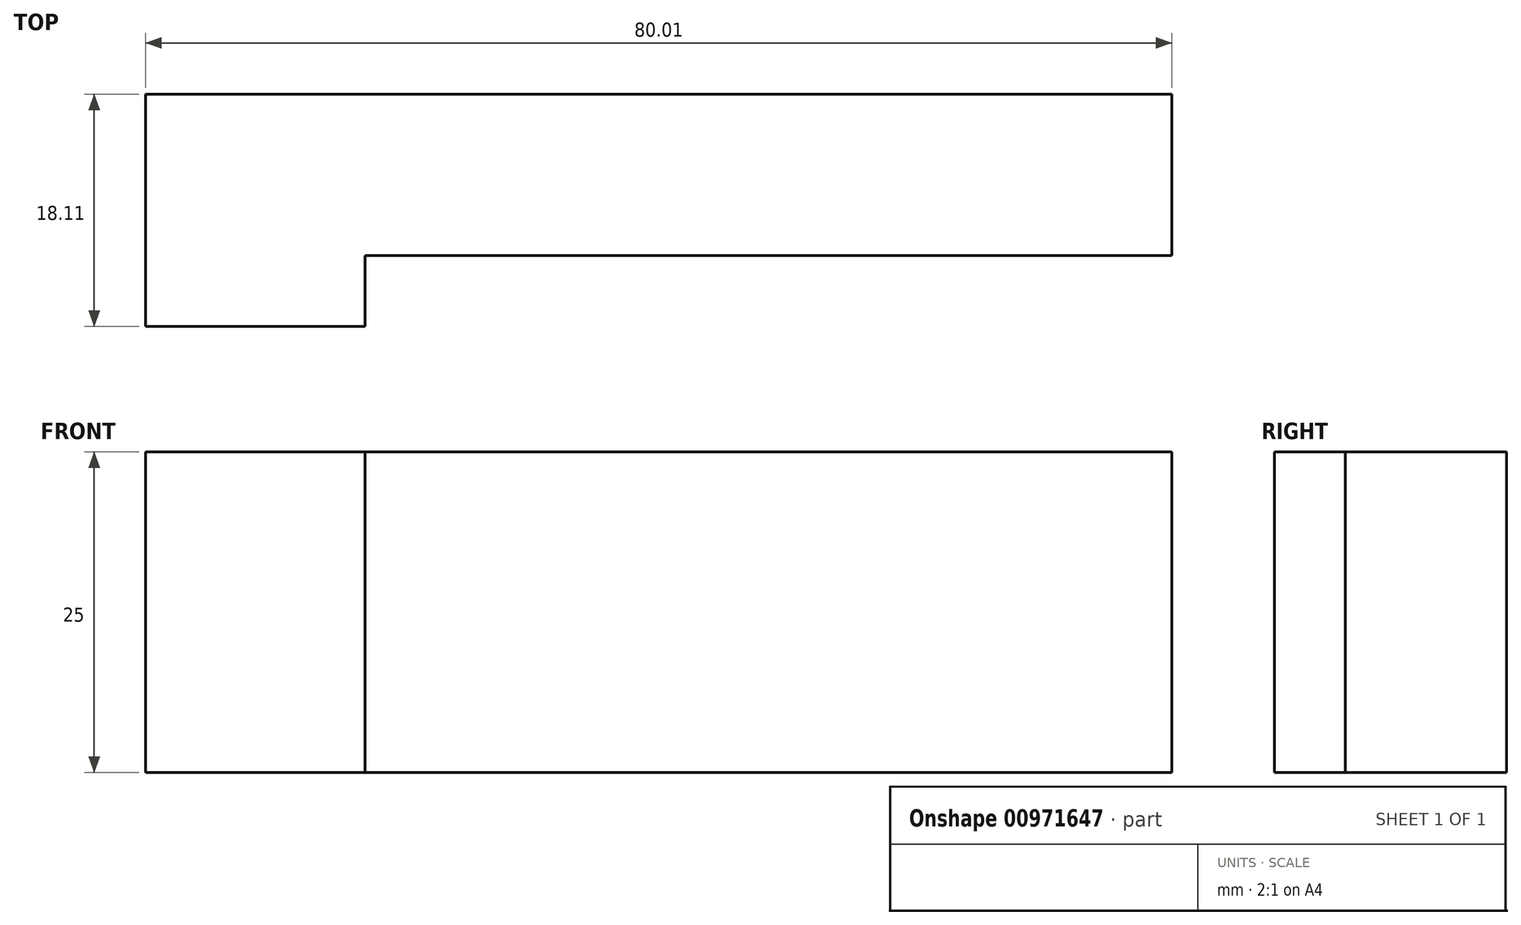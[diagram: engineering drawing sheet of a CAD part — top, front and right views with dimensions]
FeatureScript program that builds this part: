
annotation { "Feature Type Name" : "Feature", "Feature Type Description" : "" }
export const myFeature = defineFeature(function(context is Context, id is Id, definition is map)
    precondition{}
    {
        {
            var Q0;
            Q0=qCreatedBy(makeId("Top.planeOp"),FACE);
            var sketch = newSketch(context, id + "F0", { "sketchPlane" : qUnion([Q0])});
            skLineSegment(sketch, "E0", {"start": v(-47.3, 0) * mm, "end": v(48.04, 0) * mm});
            skLineSegment(sketch, "E1", {"start": v(-47.3, 0) * mm, "end": v(-47.3, -18.1) * mm});
            skLineSegment(sketch, "E2", {"start": v(-47.3, -18.1) * mm, "end": v(-30.2, -18.1) * mm});
            skLineSegment(sketch, "E3", {"start": v(-30.2, -18.1) * mm, "end": v(-30.2, -12.58) * mm});
            skLineSegment(sketch, "E4", {"start": v(-30.2, -12.58) * mm, "end": v(32.7, -12.58) * mm});
            skLineSegment(sketch, "E5", {"start": v(32.7, -12.58) * mm, "end": v(32.7, 0.02) * mm});
            skSolve(sketch);
        }
        {
            var Q0;
            Q0 = qSketchRegion(id + "F0", true);
            extrude(context, id + "F1", {"entities" : qUnion([Q0]), "endBound" : BoundingType.SYMMETRIC, "depth" : 25 * mm, "offsetDistance" : 25 * mm});
        }
    });
